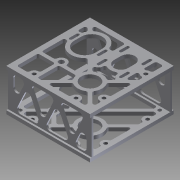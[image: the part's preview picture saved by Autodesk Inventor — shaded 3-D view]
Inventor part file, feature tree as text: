
AUTODESK INVENTOR PART (.ipt)
format: ipt  version: 2012 (Build 160160000, 160)  size: 899,072 bytes
history: native  units: in
note: dims shown in document units (in); Inventor stores cm internally (conversion verified against a paired STEP export)
features: thread x8, extrude x7, sketch x5, fillet x3, projected_geometry x1
ambient origin geometry x8: Origin, YZ Plane, XZ Plane, XY Plane, X Axis, Y Axis, Z Axis, Center Point
bodies: Solid1 (feature_tree)
feature tree (24):
  extrude  "Extrusion1"  Depth=0.1875in
  sketch  "Sketch2"  dims[d4=0.25in d5=0.25in d6=6.0in d7=0.0in]
  extrude  "Extrusion2"  Depth=6.0in TaperAngle=0.0deg
  extrude  "Extrusion3"  Depth=1.25in
  extrude  "Extrusion4"  Depth=1.625in
  fillet  "Fillet2"  Radius=0.375in
  sketch  "Sketch6"  dims[d20=0.25in d21=0.125in d22=0.25in d24=0.25in d25=0.125in d27=0.125in d32=0.25in d33=0.0in d35=0.375in d36=0.375in d37=0.375in d38=0.375in d39=0.1719in d40=0.3438in d41=0.3438in d42=0.3438in d43=0.3438in d44=0.125in d46=0.125in d49=0.125in d50=0.125in d51=0.125in d52=0.125in d53=0.125in d54=0.125in d55=0.125in d56=0.125in d57=0.25in d58=0.0in d60=0.3278in d61=0.3278in d62=0.3278in d63=0.3278in d64=0.125in d65=0.125in d66=0.125in d67=0.125in d68=0.125in d69=0.125in d70=0.125in d71=0.125in d72=0.125in d73=0.125in d74=0.375in d76=0.25in d77=0.375in d78=0.375in d79=0.25in d80=0.0in d81=0.25in d88=0.125in d89=1.25in d90=1.5in d91=0.75in d92=0.5in d94=0.2in d96=0.9in d97=1.0in d98=0.5in d99=0.5in d101=2.0in d102=0.2in d103=0.8in d104=0.8in d105=0.7874in d107=1.6in d108=0.7874in d110=1.6in d114=1.0in d115=1.0in d116=1.625in d117=1.0in d119=0.2in d122=4.5in d123=1.3125in d124=0.366in d126=2.3in d127=0.25in d128=0.0in d129=0.375in d131=4.5in d132=0.125in d153=0.25in d154=0.125in d156=0.375in d157=0.375in d160=0.25in d161=0.125in d162=0.25in d163=0.125in d165=0.875in d166=0.125in d169=0.25in d170=0.125in d171=1.0in d172=0.25in d177=0.125in d178=0.6in d179=0.25in d180=0.0in d181=0.125in d183=0.25in d185=0.25in d186=0.125in d188=1.5625in d190=1.3125in d191=0.366in d193=0.25in d194=0.125in d197=1.0in d198=1.176in d199=0.1in d200=0.0in d201=0.125in d203=0.25in d204=0.25in d205=0.125in d207=2.1875in d208=2.0312in d211=0.125in d212=0.3in d213=0.5in d214=0.25in d215=0.3125in d220=0.5in d221=1.5in d222=0.25in d224=0.1875in d225=2.3in d226=0.35in d227=0.25in d228=1.5in d229=1.5in d230=0.5821in d231=0.25in d232=1.5in d233=0.125in d234=0.25in d235=2.0in d236=0.25in d237=1.5in d238=0.3125in d239=0.7874in d241=3.0in d242=0.3937in d244=1.0in d246=1.5in d247=0.7874in d249=3.0in d250=0.3937in d252=1.0in d254=0.5in d255=0.25in d256=0.3125in d257=0.25in d258=0.5in d259=0.3125in d260=0.25in d262=0.75in d264=6.0in d267=0.25in d269=3.0in d270=6.0in d272=0.25in d273=0.125in d274=0.125in d275=0.1639in d277=1.0in d278=0.0in d279=1.0in d280=0.0in d281=1.0in d282=0.0in d283=1.0in d284=0.0in d285=1.0in d286=0.0in d287=1.0in d288=0.0in d289=1.0in d290=0.0in d291=1.0in d292=0.0in d293=0.125in d294=0.125in d295=0.125in d296=0.75in d297=0.4837in d298=0.375in]
  fillet  "Fillet3"  Radius=0.875in
  extrude  "Extrusion5"  Depth=0.125in
  extrude  "Extrusion6"  Depth=0.25in
  fillet  "Fillet4"  Radius=0.25in
  extrude  "Extrusion7"  Depth=0.125in
  thread  "Thread1"  [1 undecoded]
  thread  "Thread2"  [1 undecoded]
  thread  "Thread3"  [1 undecoded]
  thread  "Thread4"  [1 undecoded]
  thread  "Thread5"  [1 undecoded]
  thread  "Thread6"  [1 undecoded]
  thread  "Thread7"  [1 undecoded]
  thread  "Thread8"  [1 undecoded]
  sketch  "Sketch1"  dims[d1=3.0in d2=0.1875in d3=0.25in]
  sketch  "Sketch4"  dims[d11=2.0312in d13=1.25in]
  sketch  "Sketch5"  dims[d15=2.625in d16=1.625in d18=0.375in d19=0.875in]
  projected_geometry  "Projected Loop1"
note: 8 required parameter values undecoded (feature->parameter linkage not recoverable at this tier; creation-order binding heuristic only, values carry confidence <= 0.55)
